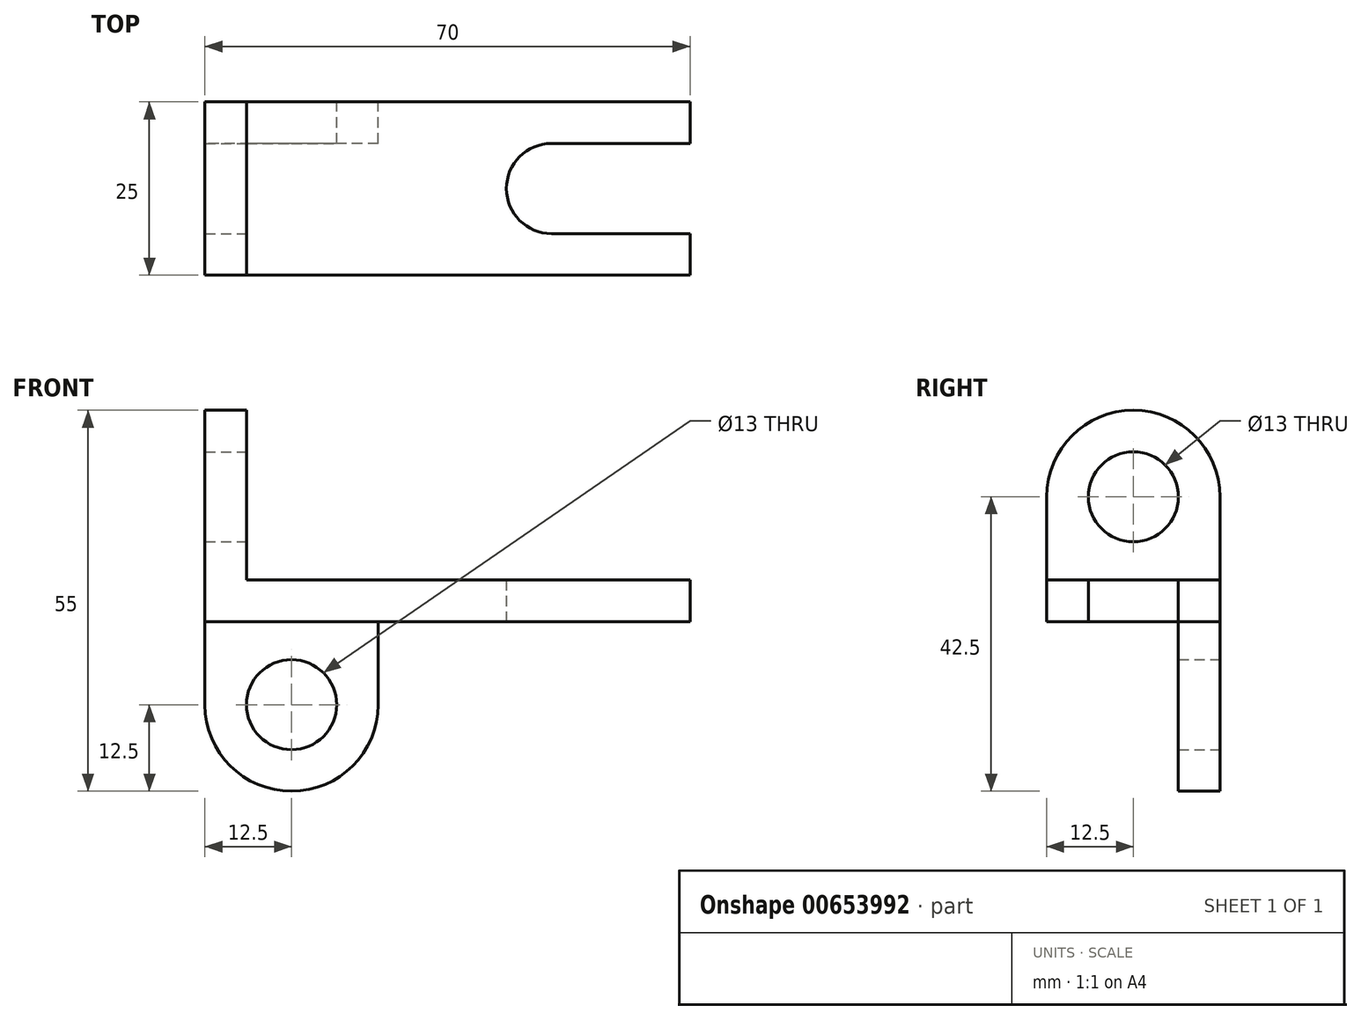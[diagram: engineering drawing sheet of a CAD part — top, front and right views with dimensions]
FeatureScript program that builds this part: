
annotation { "Feature Type Name" : "Feature", "Feature Type Description" : "" }
export const myFeature = defineFeature(function(context is Context, id is Id, definition is map)
    precondition{}
    {
        {
            var Q0;
            Q0=qCreatedBy(makeId("Top.planeOp"),FACE);
            var sketch = newSketch(context, id + "F0", { "sketchPlane" : qUnion([Q0])});
            skLineSegment(sketch, "E0.bottom", {"start": v(32, 12.5) * mm, "end": v(-32, 12.5) * mm});
            skLineSegment(sketch, "E0.top", {"start": v(32, -12.5) * mm, "end": v(-32, -12.5) * mm});
            skLineSegment(sketch, "E0.left", {"start": v(32, 12.5) * mm, "end": v(32, -12.5) * mm});
            skLineSegment(sketch, "E0.right", {"start": v(-32, 12.5) * mm, "end": v(-32, -12.5) * mm});
            skPoint(sketch, "E0.middle", {"position": v(0, 0) * mm});
            skLineSegment(sketch, "E1.bottom", {"start": v(32, 6.5) * mm, "end": v(12, 6.5) * mm});
            skLineSegment(sketch, "E1.top", {"start": v(32, -6.5) * mm, "end": v(12, -6.5) * mm});
            skLineSegment(sketch, "E1.left", {"start": v(32, 6.5) * mm, "end": v(32, -6.5) * mm});
            skLineSegment(sketch, "E1.right", {"start": v(12, 6.5) * mm, "end": v(12, -6.5) * mm});
            skPoint(sketch, "E1.middle", {"position": v(22, 0) * mm});
            skCircle(sketch, "E2", {"center": v(12, 0) * mm, "radius": 6.5 * mm});
            skSolve(sketch);
        }
        {
            var Q0;
            {var subQ4=sQuery(id+"F0.wireOp",EDGE,"E0.bottom");Q0=makeQuery(id+"F0.imprint","IMPRINT",FACE,{"disambiguationData":[TD([[makeQuery(id+"F0.imprint","IMPRINT",EDGE,{"derivedFrom":subQ4}),1.0]])]});}
            extrude(context, id + "F1", {"entities" : qUnion([Q0]), "depth" : 6 * mm, "offsetDistance" : 25 * mm});
        }
        {
            var Q0;
            Q0=makeQuery(id+"F1.opExtrude","SWEPT_FACE",FACE,{"disambiguationData":[OSD([sQuery(id+"F0.wireOp",EDGE,"E0.right")])]});
            var sketch = newSketch(context, id + "F2", { "sketchPlane" : qUnion([Q0])});
            skLineSegment(sketch, "E3.bottom", {"start": v(-12.5, 0) * mm, "end": v(12.5, 0) * mm});
            skLineSegment(sketch, "E3.top", {"start": v(-12.5, 18) * mm, "end": v(12.5, 18) * mm});
            skLineSegment(sketch, "E3.left", {"start": v(-12.5, 0) * mm, "end": v(-12.5, 18) * mm});
            skLineSegment(sketch, "E3.right", {"start": v(12.5, 0) * mm, "end": v(12.5, 18) * mm});
            skCircle(sketch, "E4", {"center": v(0, 18) * mm, "radius": 12.5 * mm});
            skCircle(sketch, "E5", {"center": v(0, 18) * mm, "radius": 6.5 * mm});
            skSolve(sketch);
        }
        {
            var Q0;
            Q0 = qSketchRegion(id + "F2", true);
            extrude(context, id + "F3", {"entities" : qUnion([Q0]), "operationType" : NewBodyOperationType.ADD, "depth" : 6 * mm, "offsetDistance" : 25 * mm});
        }
        {
            var Q0;
            Q0=makeQuery(id+"F3.boolean.opBoolean","MERGE",FACE,{"derivedFrom":[makeQuery(id+"F1.opExtrude","SWEPT_FACE",FACE,{"disambiguationData":[OSD([sQuery(id+"F0.wireOp",EDGE,"E0.bottom")])]}),makeQuery(id+"F3.opExtrude","SWEPT_FACE",FACE,{"disambiguationData":[OSD([sQuery(id+"F2.wireOp",EDGE,"E3.left")])]})]});
            var sketch = newSketch(context, id + "F4", { "sketchPlane" : qUnion([Q0])});
            skLineSegment(sketch, "E6.bottom", {"start": v(38, 0) * mm, "end": v(13, 0) * mm});
            skLineSegment(sketch, "E6.top", {"start": v(38, -12) * mm, "end": v(13, -12) * mm});
            skLineSegment(sketch, "E6.left", {"start": v(38, 0) * mm, "end": v(38, -12) * mm});
            skLineSegment(sketch, "E6.right", {"start": v(13, 0) * mm, "end": v(13, -12) * mm});
            skCircle(sketch, "E7", {"center": v(25.5, -12) * mm, "radius": 12.5 * mm});
            skCircle(sketch, "E8", {"center": v(25.5, -12) * mm, "radius": 6.5 * mm});
            skSolve(sketch);
        }
        {
            var Q0;
            Q0 = qSketchRegion(id + "F4", true);
            var Q1;
            {var subQ0=sQuery(id+"F0.wireOp",EDGE,"E0.bottom");Q1=makeQuery(id+"F4.imprint","IMPRINT",FACE,{"disambiguationData":[TD([[makeQuery(id+"F4.imprint","IMPRINT",EDGE,{"derivedFrom":makeQuery(id+"F1.opExtrude","CAP_EDGE",EDGE,{"disambiguationData":[OSD([subQ0])],"isStart":false})}),-1.0]])]});}
            extrude(context, id + "F5", {"entities" : qUnion([Q0, Q1]), "operationType" : NewBodyOperationType.ADD, "oppositeDirection" : true, "depth" : 6 * mm, "offsetDistance" : 25 * mm});
        }
    });
